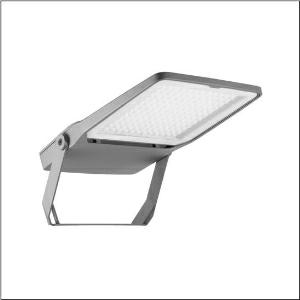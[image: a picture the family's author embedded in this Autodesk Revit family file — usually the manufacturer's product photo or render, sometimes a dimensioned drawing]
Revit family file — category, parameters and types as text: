
# Revit family: floodlight_fl_20_midi___pl43_5xa7682g2a1kc_f4ca
name_source: partatom
category: Lighting Fixtures
units: mm (PartAtom-declared; Revit-internal decimal feet)

## family parameters
Cut with Voids When Loaded = No
Host = Face
Light Source = No
Part Type = Normal
Room Calculation Point = No
Round Connector Dimension = Use Diameter
Shared = No

## types (1)
- --- (1 x LED 4000K / CRI = 70 (unbekannt), 38700 lm, 4000K)
    Apparent Load = 306 VA
    CIE Flux Codes = 32 74 99 100 100
    Color Rendering = 70
    Color Temperature = 4000K
    Default Elevation = 1800 mm
    Description = Floodlight FL 20 midi, floodlight, primary light control with lens, of plastic, primary optical cover: protective disc, of toughened safety glass, transparent, light distribution: PL43, light emission: direct distribution, primary light characteristic: asymmetric, installation type: surface-mounted, LED, High Power LED, rated luminous flux: 38.700lm, luminous efficacy: 127lm/W, light colour: 740, colour temperature: 4000K, control gear: ECG Plus, control: overheat protection, power reduction, digital communication interface, flexible luminous flux parameterisation, time-dependent luminous flux control, electronic power reduction, with terminal, 10-pole, max. 2.5mm², mains connection: 220..240V, AC, 50/60Hz, rated input power: 306W, LED unit, of diecast aluminium, powder-coated, Siteco® metallic grey (DB 702S), corrosivity category C5 mid according to DIN EN ISO 12944, length: 654mm, width: 450mm, height: 76mm, housing frame, of diecast aluminium, powder-coated, Siteco® metallic grey (DB 702S), DALI, protection rating (complete): IP66, insulation class (complete): insulation class II (safety insulation), certification: CE, ENEC, VDE, protection symbol: D, permissible operating ambient temperature: -40..+40°C, permissible operating ambient temperature for outdoor applications: -40..+50°C, standard: DIN EN 12944, packaging unit: 1 piece

Light Distribution: PL43
    Height = 76 mm
    Lamp = 1 x LED 4000K / CRI >= 70 (unbekannt)
    Lamp Light Flux = 38700 lm
    Lamp count = 1
    Length = 672 mm
    Luminous efficacy = 127 lm/W
    Manufacturer = Siteco
    ModVariant = No
    Model = 5XA7682G2A1KC
    Number of Poles = 1
    OnlyDefault = Yes
    Power Factor = 1
    Product Name = Floodlight FL 20 midi | PL43
    Product group = floodlight | pylon annexe
    ProductGroupID = 6200
    Protection Class = Protection class II
    Protection Degree = IP 66
    RLX_Detail_Level = 1
    RLX_Emergency_Light_Flux = 0 lm
    RLX_Emergency_Type = 0
    RLX_Emergency_Type_DB = No
    RlxData = <blob elided: 97461 chars, md5=f64b4330>
    Socket = socket
    Standby Power = 0 W
    System Light Flux = 38700 lm
    System Power = 306 W
    Type Comments = factory setting: luminous flux: 100 % | dim-lin: 254 | 700 mA
    Type Image = l_1005943.jpg
    URL = http://relux.com
    VarID = @adj_148113
    Voltage = 0 V
    Weight = 0.00 kg
    Width = 450 mm

## geometry (parser evidence)
native form markers: Blend x4, Sweep x11
no freeform markers — native parametric forms only
